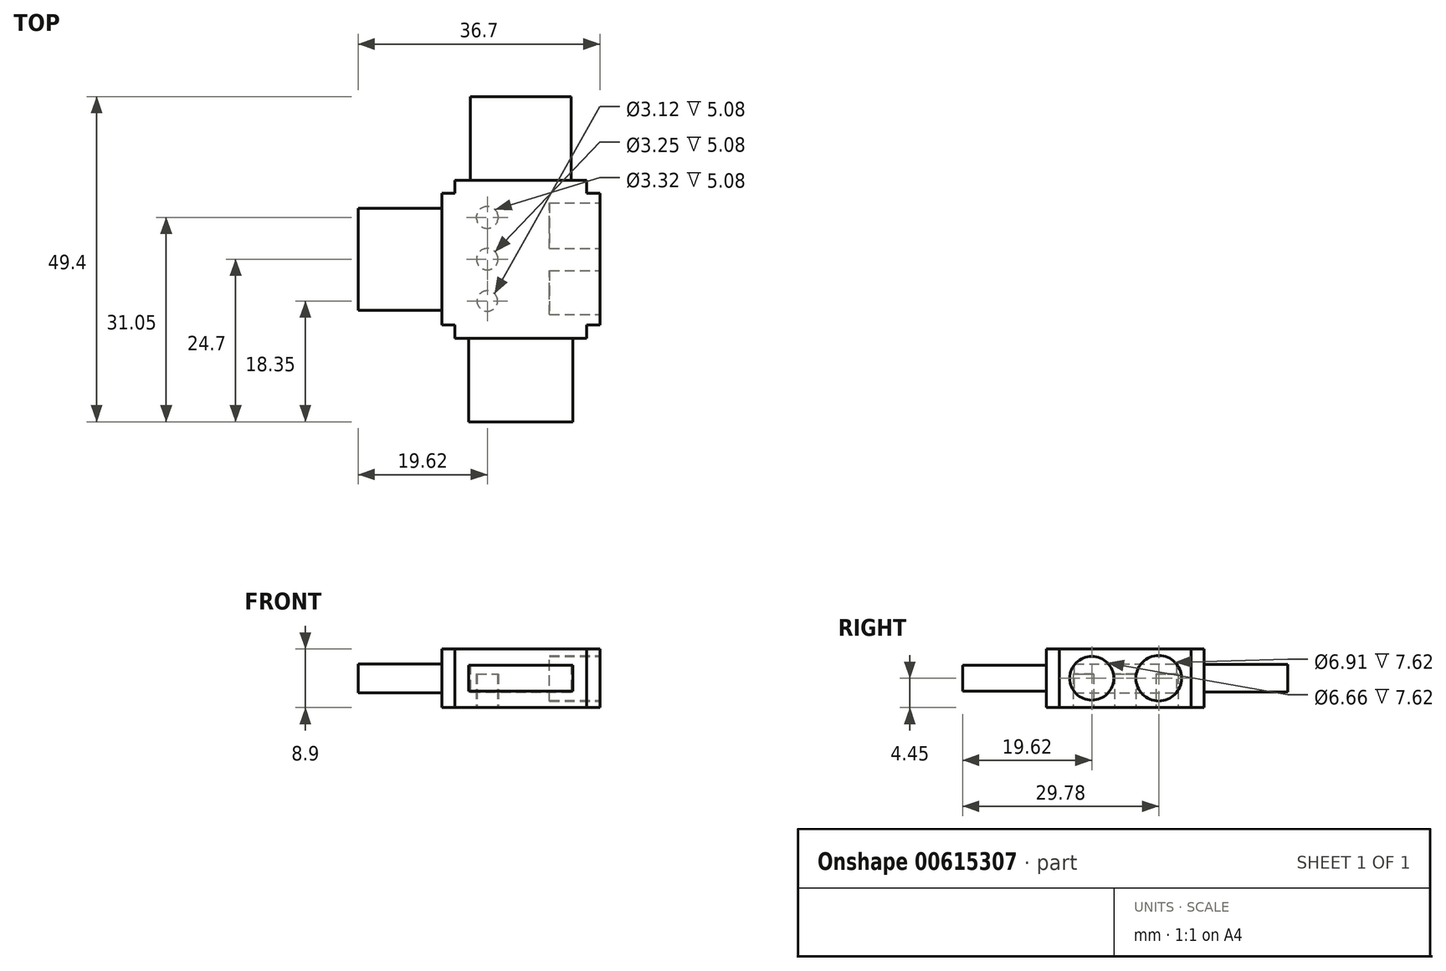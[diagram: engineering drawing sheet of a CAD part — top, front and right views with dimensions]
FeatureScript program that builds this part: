
annotation { "Feature Type Name" : "Feature", "Feature Type Description" : "" }
export const myFeature = defineFeature(function(context is Context, id is Id, definition is map)
    precondition{}
    {
        {
            var Q0;
            Q0=qCreatedBy(makeId("Top.planeOp"),FACE);
            var sketch = newSketch(context, id + "F0", { "sketchPlane" : qUnion([Q0])});
            skLineSegment(sketch, "E0.bottom", {"start": v(10, 12) * mm, "end": v(-10, 12) * mm});
            skLineSegment(sketch, "E0.top", {"start": v(10, -12) * mm, "end": v(-10, -12) * mm});
            skLineSegment(sketch, "E0.left", {"start": v(10, 12) * mm, "end": v(10, -12) * mm});
            skLineSegment(sketch, "E0.right", {"start": v(-10, 12) * mm, "end": v(-10, -12) * mm});
            skPoint(sketch, "E0.middle", {"position": v(0, 0) * mm});
            skLineSegment(sketch, "E1.bottom", {"start": v(-12, 10) * mm, "end": v(12, 10) * mm});
            skLineSegment(sketch, "E1.top", {"start": v(-12, -10) * mm, "end": v(12, -10) * mm});
            skLineSegment(sketch, "E1.left", {"start": v(-12, 10) * mm, "end": v(-12, -10) * mm});
            skLineSegment(sketch, "E1.right", {"start": v(12, 10) * mm, "end": v(12, -10) * mm});
            skSolve(sketch);
        }
        {
            var Q0;
            Q0 = qSketchRegion(id + "F0", true);
            extrude(context, id + "F1", {"entities" : qUnion([Q0]), "endBound" : BoundingType.SYMMETRIC, "depth" : 8.9 * mm, "offsetDistance" : 25.4 * mm});
        }
        {
            var Q0;
            Q0=makeQuery(id+"F1.opExtrude","SWEPT_FACE",FACE,{"disambiguationData":[OSD([sQuery(id+"F0.wireOp",EDGE,"E1.left")])]});
            var sketch = newSketch(context, id + "F2", { "sketchPlane" : qUnion([Q0])});
            skLineSegment(sketch, "E2.bottom", {"start": v(7.75, 2.2) * mm, "end": v(-7.75, 2.2) * mm});
            skLineSegment(sketch, "E2.top", {"start": v(7.75, -2.2) * mm, "end": v(-7.75, -2.2) * mm});
            skLineSegment(sketch, "E2.left", {"start": v(7.75, 2.2) * mm, "end": v(7.75, -2.2) * mm});
            skLineSegment(sketch, "E2.right", {"start": v(-7.75, 2.2) * mm, "end": v(-7.75, -2.2) * mm});
            skPoint(sketch, "E2.middle", {"position": v(0, 0) * mm});
            skSolve(sketch);
        }
        {
            var Q0;
            Q0=makeQuery(id+"F2.imprint","IMPRINT",FACE,{"disambiguationData":[TD([[makeQuery(id+"F2.imprint","IMPRINT",EDGE,{"derivedFrom":sQuery(id+"F2.wireOp",EDGE,"E2.bottom")}),1.0]])]});
            extrude(context, id + "F3", {"entities" : qUnion([Q0]), "operationType" : NewBodyOperationType.ADD, "depth" : 12.7 * mm, "offsetDistance" : 25.4 * mm});
        }
        {
            var Q0;
            Q0=makeQuery(id+"F1.opExtrude","SWEPT_FACE",FACE,{"disambiguationData":[OSD([sQuery(id+"F0.wireOp",EDGE,"E0.top")])]});
            var sketch = newSketch(context, id + "F4", { "sketchPlane" : qUnion([Q0])});
            skLineSegment(sketch, "E3.bottom", {"start": v(-7.88, -1.95) * mm, "end": v(7.87, -1.95) * mm});
            skLineSegment(sketch, "E3.top", {"start": v(-7.87, 1.95) * mm, "end": v(7.88, 1.95) * mm});
            skLineSegment(sketch, "E3.left", {"start": v(-7.87, 1.95) * mm, "end": v(-7.88, -1.95) * mm});
            skLineSegment(sketch, "E3.right", {"start": v(7.88, 1.95) * mm, "end": v(7.88, -1.95) * mm});
            skPoint(sketch, "E3.middle", {"position": v(0, 0) * mm});
            skSolve(sketch);
        }
        {
            var Q0;
            Q0 = qSketchRegion(id + "F4", true);
            extrude(context, id + "F5", {"entities" : qUnion([Q0]), "operationType" : NewBodyOperationType.ADD, "depth" : 12.7 * mm, "offsetDistance" : 25.4 * mm});
        }
        {
            var Q0;
            Q0=makeQuery(id+"F1.opExtrude","SWEPT_FACE",FACE,{"disambiguationData":[OSD([sQuery(id+"F0.wireOp",EDGE,"E0.bottom")])]});
            var sketch = newSketch(context, id + "F6", { "sketchPlane" : qUnion([Q0])});
            skLineSegment(sketch, "E4.bottom", {"start": v(7.62, 2.07) * mm, "end": v(-7.62, 2.07) * mm});
            skLineSegment(sketch, "E4.top", {"start": v(7.62, -2.07) * mm, "end": v(-7.62, -2.07) * mm});
            skLineSegment(sketch, "E4.left", {"start": v(7.62, 2.07) * mm, "end": v(7.62, -2.07) * mm});
            skLineSegment(sketch, "E4.right", {"start": v(-7.62, 2.07) * mm, "end": v(-7.62, -2.07) * mm});
            skPoint(sketch, "E4.middle", {"position": v(0, 0) * mm});
            skSolve(sketch);
        }
        {
            var Q0;
            Q0 = qSketchRegion(id + "F6", true);
            extrude(context, id + "F7", {"entities" : qUnion([Q0]), "operationType" : NewBodyOperationType.ADD, "depth" : 12.7 * mm, "offsetDistance" : 25.4 * mm});
        }
        {
            var Q0;
            Q0=makeQuery(id+"F1.opExtrude","SWEPT_FACE",FACE,{"disambiguationData":[OSD([sQuery(id+"F0.wireOp",EDGE,"E1.right")])]});
            var sketch = newSketch(context, id + "F8", { "sketchPlane" : qUnion([Q0])});
            skCircle(sketch, "E5", {"center": v(-5.08, 0) * mm, "radius": 3.33 * mm});
            skCircle(sketch, "E6", {"center": v(5.08, 0) * mm, "radius": 3.46 * mm});
            skSolve(sketch);
        }
        {
            var Q0;
            Q0 = qSketchRegion(id + "F8", true);
            extrude(context, id + "F9", {"entities" : qUnion([Q0]), "operationType" : NewBodyOperationType.REMOVE, "oppositeDirection" : true, "depth" : 7.62 * mm, "offsetDistance" : 25.4 * mm});
        }
        {
            var Q0;
            Q0=makeQuery(id+"F1.opExtrude","CAP_FACE",FACE,{"disambiguationData":[OSD([sQuery(id+"F0.wireOp",EDGE,"E0.bottom"),sQuery(id+"F0.wireOp",EDGE,"E0.top"),sQuery(id+"F0.wireOp",EDGE,"E0.left"),sQuery(id+"F0.wireOp",EDGE,"E0.right"),sQuery(id+"F0.wireOp",EDGE,"E1.bottom"),sQuery(id+"F0.wireOp",EDGE,"E1.top"),sQuery(id+"F0.wireOp",EDGE,"E1.left"),sQuery(id+"F0.wireOp",EDGE,"E1.right")])],"isStart":true});
            var sketch = newSketch(context, id + "F10", { "sketchPlane" : qUnion([Q0])});
            skCircle(sketch, "E7", {"center": v(-5.08, -6.35) * mm, "radius": 1.66 * mm});
            skCircle(sketch, "E8", {"center": v(-5.08, 0) * mm, "radius": 1.63 * mm});
            skCircle(sketch, "E9", {"center": v(-5.08, 6.35) * mm, "radius": 1.56 * mm});
            skSolve(sketch);
        }
        {
            var Q0;
            Q0 = qSketchRegion(id + "F10", true);
            extrude(context, id + "F11", {"entities" : qUnion([Q0]), "operationType" : NewBodyOperationType.REMOVE, "oppositeDirection" : true, "depth" : 5.08 * mm, "offsetDistance" : 25.4 * mm});
        }
    });
